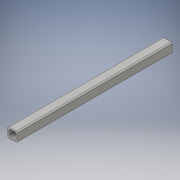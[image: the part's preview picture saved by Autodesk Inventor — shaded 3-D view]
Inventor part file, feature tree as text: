
AUTODESK INVENTOR PART (.ipt)
format: ipt  version: 2016 (Build 200138000, 138)  size: 114,688 bytes
history: native  units: in
note: dims shown in document units (in); Inventor stores cm internally (conversion verified against a paired STEP export)
features: extrude x1, sketch x1
ambient origin geometry x8: Origin, YZ Plane, XZ Plane, XY Plane, X Axis, Y Axis, Z Axis, Center Point
bodies: Solid1 (feature_tree)
feature tree (2):
  extrude  "Extrusion1"  Depth=1.0in
  sketch  "Sketch1"  dims[d0=1.0in d1=1.0in d2=0.125in d3=0.125in d4=16.0in d5=0.0in]
